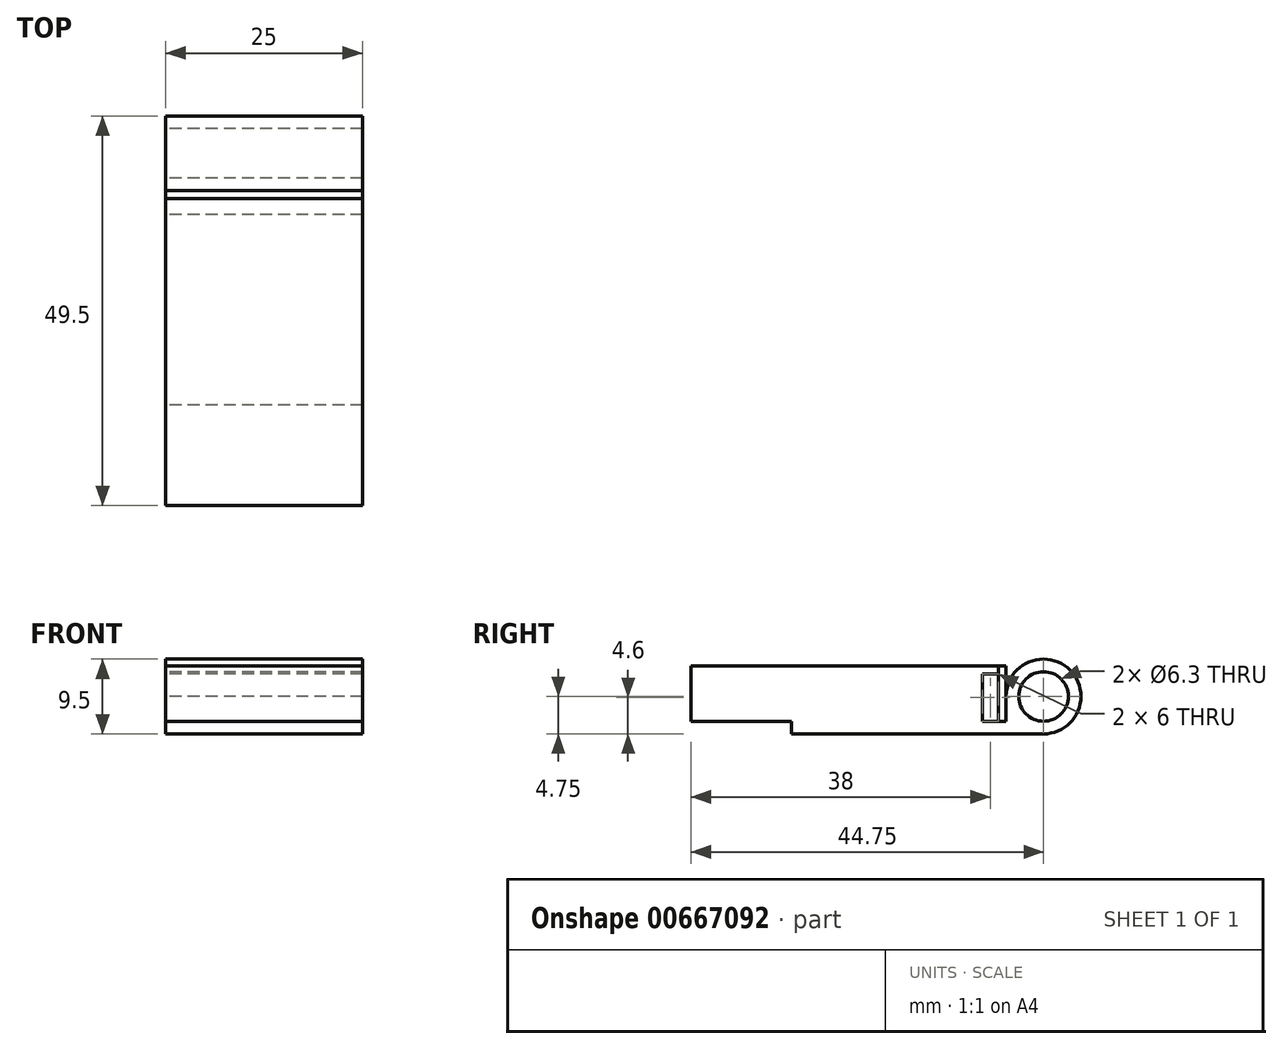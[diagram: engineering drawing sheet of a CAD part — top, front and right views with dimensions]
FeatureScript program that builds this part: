
annotation { "Feature Type Name" : "Feature", "Feature Type Description" : "" }
export const myFeature = defineFeature(function(context is Context, id is Id, definition is map)
    precondition{}
    {
        {
            var Q0;
            Q0=qCreatedBy(makeId("Right.planeOp"),FACE);
            var sketch = newSketch(context, id + "F0", { "sketchPlane" : qUnion([Q0])});
            skLineSegment(sketch, "E0.bottom", {"start": v(6.95, 0) * mm, "end": v(506.95, 0) * mm});
            skLineSegment(sketch, "E0.top", {"start": v(6.95, 7) * mm, "end": v(506.95, 7) * mm});
            skLineSegment(sketch, "E0.left", {"start": v(6.95, 0) * mm, "end": v(6.95, 7) * mm});
            skLineSegment(sketch, "E0.right", {"start": v(506.95, 0) * mm, "end": v(506.95, 7) * mm});
            skLineSegment(sketch, "E1.bottom", {"start": v(-4.75, 0) * mm, "end": v(-44.75, 0) * mm});
            skLineSegment(sketch, "E1.top", {"start": v(-4.75, 8) * mm, "end": v(-44.75, 8) * mm});
            skLineSegment(sketch, "E1.left", {"start": v(-4.75, 0) * mm, "end": v(-4.75, 8) * mm});
            skLineSegment(sketch, "E1.right", {"start": v(-44.75, 0) * mm, "end": v(-44.75, 8) * mm});
            skCircle(sketch, "E2", {"center": v(0, 3.15) * mm, "radius": 3.15 * mm});
            skArc(sketch, "E3.0", {"start": v(0, -1.6) * mm, "mid": v(1.95, 7.48) * mm, "end": v(-3.56, 0) * mm});
            skLineSegment(sketch, "E4.bottom", {"start": v(-3.56, 0) * mm, "end": v(-32, 0) * mm});
            skLineSegment(sketch, "E4.top", {"start": v(0, -1.6) * mm, "end": v(-32, -1.6) * mm});
            skLineSegment(sketch, "E4.right", {"start": v(-32, 0) * mm, "end": v(-32, -1.6) * mm});
            skLineSegment(sketch, "E5", {"start": v(-7.75, 8) * mm, "end": v(-7.75, 0) * mm});
            skLineSegment(sketch, "E6", {"start": v(-44.75, 7) * mm, "end": v(-4.75, 7) * mm});
            skLineSegment(sketch, "E7", {"start": v(-44.75, 6) * mm, "end": v(-4.75, 6) * mm});
            skLineSegment(sketch, "E8", {"start": v(-5.75, 8) * mm, "end": v(-5.75, 0) * mm});
            skSolve(sketch);
        }
        {
            var Q0;
            Q0=makeQuery(id+"F0.imprint","IMPRINT",FACE,{"disambiguationData":[TD([[makeQuery(id+"F0.imprint","IMPRINT",EDGE,{"derivedFrom":sQuery(id+"F0.wireOp",EDGE,"E2")}),-1.0]])]});
            var Q1;
            {var subQ1=sQuery(id+"F0.wireOp",EDGE,"E1.bottom");Q1=makeQuery(id+"F0.imprint","IMPRINT",FACE,{"disambiguationData":[TD([[makeQuery(id+"F0.imprint","IMPRINT",EDGE,{"derivedFrom":subQ1}),-1.0]])]});}
            var Q2;
            {var subQ0=sQuery(id+"F0.wireOp",EDGE,"E6");var subQ1=sQuery(id+"F0.wireOp",EDGE,"E1.right");var subQ2=makeQuery(id+"F0.imprint","INTERSECT",VERTEX,{"derivedFrom":[subQ1,subQ0]});Q2=makeQuery(id+"F0.imprint","IMPRINT",FACE,{"disambiguationData":[TD([[makeQuery(id+"F0.imprint","IMPRINT",EDGE,{"disambiguationData":[TD([[subQ2,1.0]])],"derivedFrom":subQ1}),-1.0]])]});}
            var Q3;
            {var subQ0=sQuery(id+"F0.wireOp",EDGE,"E6");var subQ1=sQuery(id+"F0.wireOp",EDGE,"E5");var subQ2=makeQuery(id+"F0.imprint","INTERSECT",VERTEX,{"derivedFrom":[subQ1,subQ0]});Q3=makeQuery(id+"F0.imprint","IMPRINT",FACE,{"disambiguationData":[TD([[makeQuery(id+"F0.imprint","IMPRINT",EDGE,{"disambiguationData":[TD([[subQ2,-1.0]])],"derivedFrom":subQ1}),1.0]])]});}
            var Q4;
            {var subQ0=sQuery(id+"F0.wireOp",EDGE,"E5");var subQ1=sQuery(id+"F0.wireOp",EDGE,"E4.bottom");var subQ2=makeQuery(id+"F0.imprint","INTERSECT",VERTEX,{"derivedFrom":[subQ1,subQ0]});Q4=makeQuery(id+"F0.imprint","IMPRINT",FACE,{"disambiguationData":[TD([[makeQuery(id+"F0.imprint","IMPRINT",EDGE,{"disambiguationData":[TD([[subQ2,1.0]])],"derivedFrom":subQ1}),-1.0]])]});}
            extrude(context, id + "F1", {"entities" : qUnion([Q0, Q1, Q2, Q3, Q4]), "depth" : 25 * mm, "offsetDistance" : 25 * mm});
        }
        {
            var Q0;
            {var subQ1=sQuery(id+"F0.wireOp",EDGE,"E1.bottom");Q0=makeQuery(id+"F0.imprint","IMPRINT",FACE,{"disambiguationData":[TD([[makeQuery(id+"F0.imprint","IMPRINT",EDGE,{"derivedFrom":subQ1}),-1.0]])]});}
            var Q1;
            Q1=makeQuery(id+"F0.imprint","IMPRINT",FACE,{"disambiguationData":[TD([[makeQuery(id+"F0.imprint","IMPRINT",EDGE,{"derivedFrom":sQuery(id+"F0.wireOp",EDGE,"E2")}),-1.0]])]});
            var Q2;
            {var subQ0=sQuery(id+"F0.wireOp",EDGE,"E4.bottom");var subQ1=sQuery(id+"F0.wireOp",EDGE,"E1.left");var subQ2=makeQuery(id+"F0.imprint","INTERSECT",VERTEX,{"derivedFrom":[subQ1,subQ0]});Q2=makeQuery(id+"F0.imprint","IMPRINT",FACE,{"disambiguationData":[TD([[makeQuery(id+"F0.imprint","IMPRINT",EDGE,{"disambiguationData":[TD([[subQ2,-1.0]])],"derivedFrom":subQ1}),-1.0]])]});}
            var Q3;
            {var subQ0=sQuery(id+"F0.wireOp",EDGE,"E6");var subQ1=sQuery(id+"F0.wireOp",EDGE,"E1.right");var subQ2=makeQuery(id+"F0.imprint","INTERSECT",VERTEX,{"derivedFrom":[subQ1,subQ0]});Q3=makeQuery(id+"F0.imprint","IMPRINT",FACE,{"disambiguationData":[TD([[makeQuery(id+"F0.imprint","IMPRINT",EDGE,{"disambiguationData":[TD([[subQ2,1.0]])],"derivedFrom":subQ1}),-1.0]])]});}
            var Q4;
            {var subQ0=sQuery(id+"F0.wireOp",EDGE,"E6");var subQ1=sQuery(id+"F0.wireOp",EDGE,"E1.left");var subQ2=makeQuery(id+"F0.imprint","INTERSECT",VERTEX,{"derivedFrom":[subQ1,subQ0]});Q4=makeQuery(id+"F0.imprint","IMPRINT",FACE,{"disambiguationData":[TD([[makeQuery(id+"F0.imprint","IMPRINT",EDGE,{"disambiguationData":[TD([[subQ2,1.0]])],"derivedFrom":subQ1}),1.0]])]});}
            var Q5;
            {var subQ1=sQuery(id+"F0.wireOp",EDGE,"E4.bottom");var subQ5=sQuery(id+"F0.wireOp",EDGE,"E1.left");var subQ6=makeQuery(id+"F0.imprint","INTERSECT",VERTEX,{"derivedFrom":[subQ5,subQ1]});Q5=makeQuery(id+"F0.imprint","IMPRINT",FACE,{"disambiguationData":[TD([[makeQuery(id+"F0.imprint","IMPRINT",EDGE,{"disambiguationData":[TD([[subQ6,-1.0]])],"derivedFrom":subQ5}),1.0]])]});}
            var Q6;
            {var subQ0=sQuery(id+"F0.wireOp",EDGE,"E6");var subQ1=sQuery(id+"F0.wireOp",EDGE,"E5");var subQ2=makeQuery(id+"F0.imprint","INTERSECT",VERTEX,{"derivedFrom":[subQ1,subQ0]});Q6=makeQuery(id+"F0.imprint","IMPRINT",FACE,{"disambiguationData":[TD([[makeQuery(id+"F0.imprint","IMPRINT",EDGE,{"disambiguationData":[TD([[subQ2,-1.0]])],"derivedFrom":subQ1}),1.0]])]});}
            var Q7;
            {var subQ0=sQuery(id+"F0.wireOp",EDGE,"E5");var subQ1=sQuery(id+"F0.wireOp",EDGE,"E4.bottom");var subQ2=makeQuery(id+"F0.imprint","INTERSECT",VERTEX,{"derivedFrom":[subQ1,subQ0]});Q7=makeQuery(id+"F0.imprint","IMPRINT",FACE,{"disambiguationData":[TD([[makeQuery(id+"F0.imprint","IMPRINT",EDGE,{"disambiguationData":[TD([[subQ2,1.0]])],"derivedFrom":subQ1}),-1.0]])]});}
            extrude(context, id + "F2", {"entities" : qUnion([Q0, Q1, Q2, Q3, Q4, Q5, Q6, Q7]), "depth" : 25 * mm, "offsetDistance" : 25 * mm});
        }
    });
